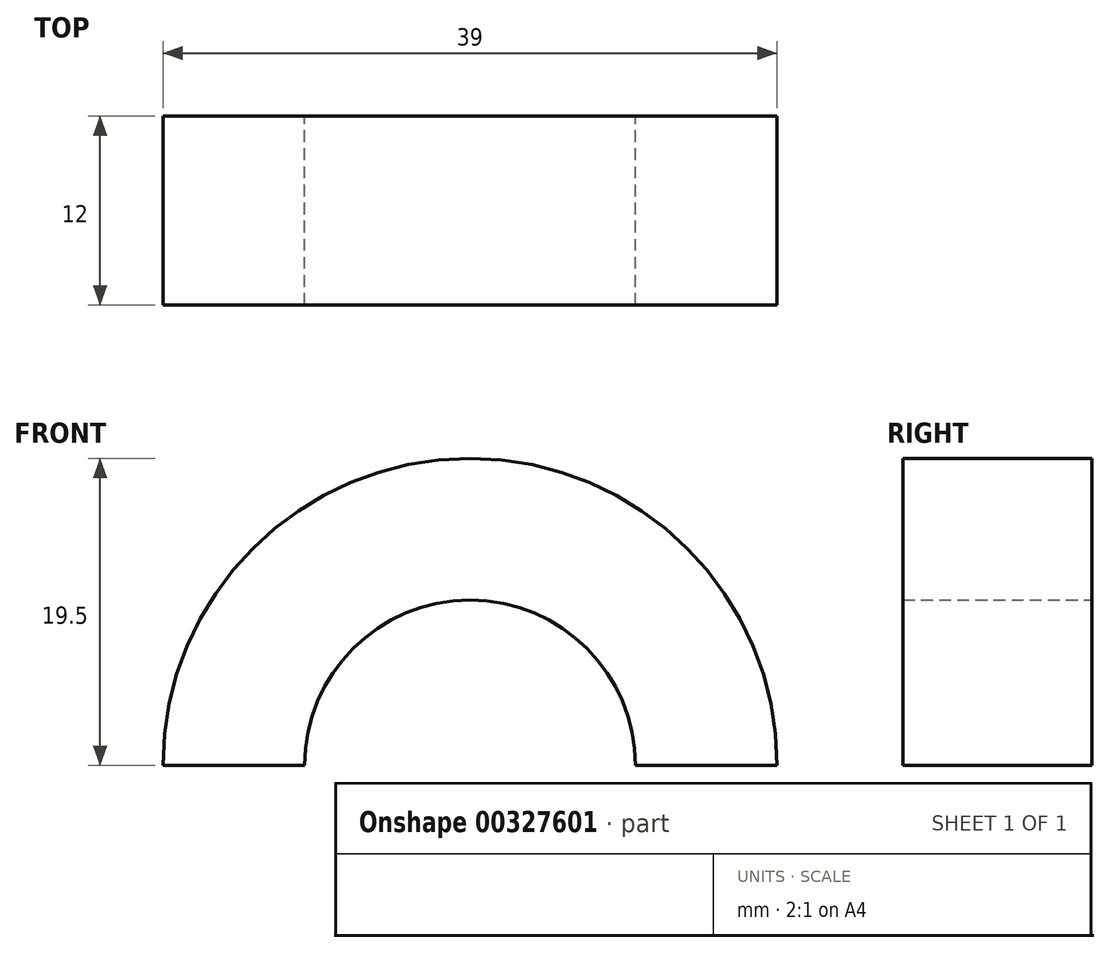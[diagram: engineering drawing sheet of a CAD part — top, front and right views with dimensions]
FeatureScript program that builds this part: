
annotation { "Feature Type Name" : "Feature", "Feature Type Description" : "" }
export const myFeature = defineFeature(function(context is Context, id is Id, definition is map)
    precondition{}
    {
        {
            var Q0;
            Q0=qCreatedBy(makeId("Front.planeOp"),FACE);
            var sketch = newSketch(context, id + "F0", { "sketchPlane" : qUnion([Q0])});
            skArc(sketch, "E0", {"start": v(10.5, 0) * mm, "mid": v(0, 10.5) * mm, "end": v(-10.5, 0) * mm});
            skArc(sketch, "E1", {"start": v(19.5, 0) * mm, "mid": v(0, 19.5) * mm, "end": v(-19.5, 0) * mm});
            skLineSegment(sketch, "E2", {"start": v(-19.5, 0) * mm, "end": v(-10.5, 0) * mm});
            skLineSegment(sketch, "E3", {"start": v(10.5, 0) * mm, "end": v(19.5, 0) * mm});
            skSolve(sketch);
        }
        {
            var Q0;
            Q0 = qSketchRegion(id + "F0", true);
            extrude(context, id + "F1", {"entities" : qUnion([Q0]), "endBound" : BoundingType.SYMMETRIC, "depth" : 12 * mm});
        }
    });
